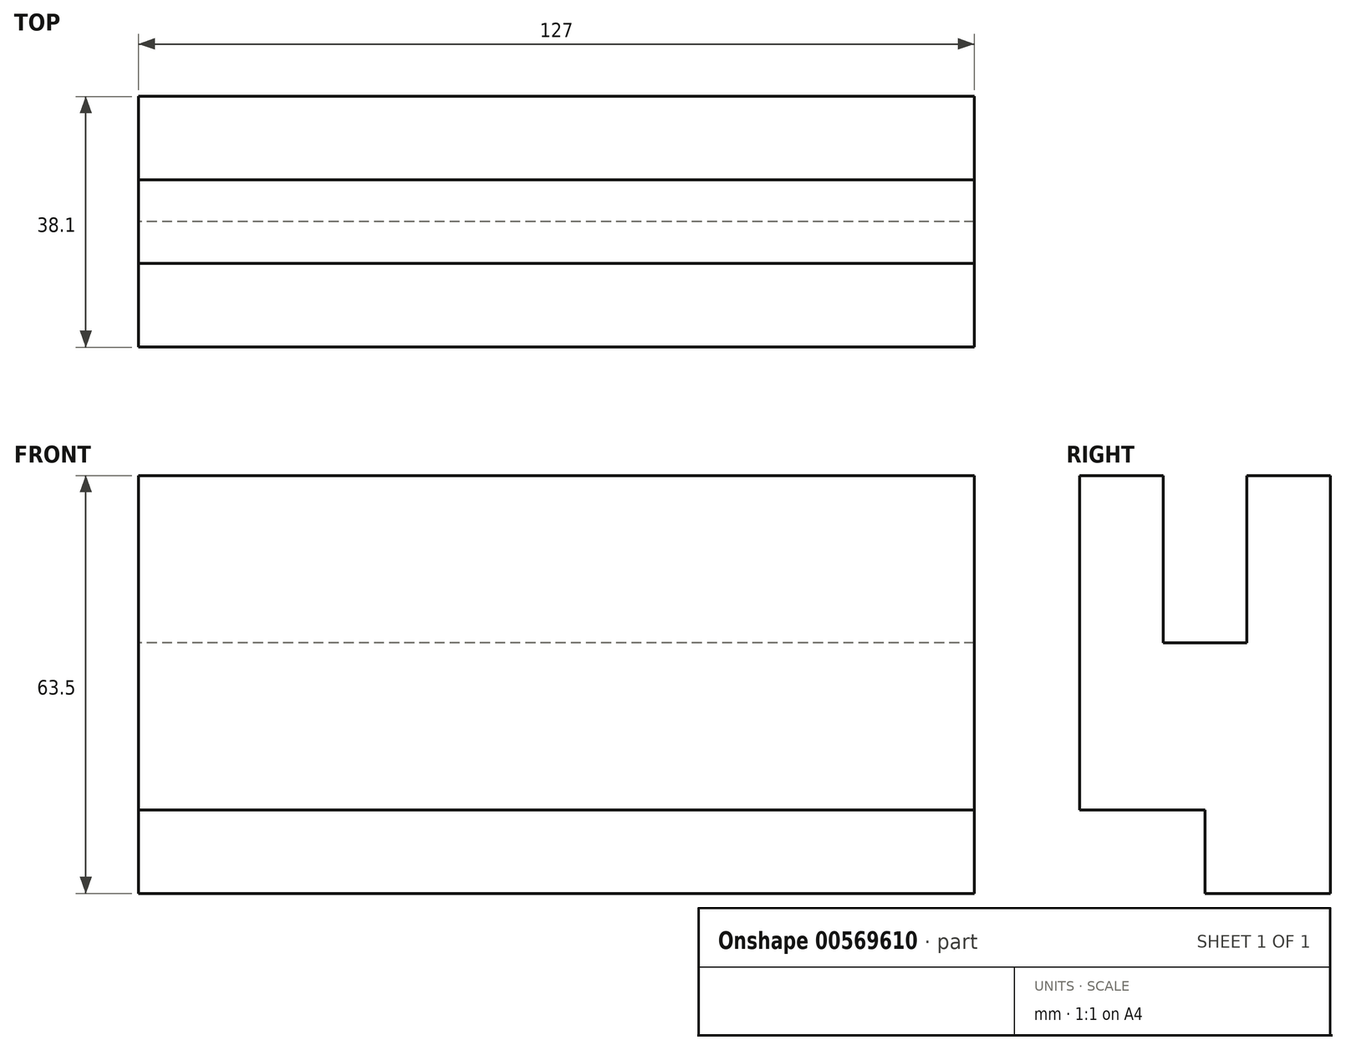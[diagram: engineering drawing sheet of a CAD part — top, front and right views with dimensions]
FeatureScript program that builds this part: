
annotation { "Feature Type Name" : "Feature", "Feature Type Description" : "" }
export const myFeature = defineFeature(function(context is Context, id is Id, definition is map)
    precondition{}
    {
        {
            var Q0;
            Q0=qCreatedBy(makeId("Right.planeOp"),FACE);
            var sketch = newSketch(context, id + "F0", { "sketchPlane" : qUnion([Q0])});
            skLineSegment(sketch, "E0", {"start": v(-39.45, 50.8) * mm, "end": v(-26.75, 50.8) * mm});
            skLineSegment(sketch, "E1", {"start": v(-26.75, 50.8) * mm, "end": v(-26.75, 25.4) * mm});
            skLineSegment(sketch, "E2", {"start": v(-14.05, 25.4) * mm, "end": v(-14.05, 50.8) * mm});
            skLineSegment(sketch, "E3", {"start": v(-14.05, 50.8) * mm, "end": v(-14.05, 25.4) * mm});
            skLineSegment(sketch, "E4", {"start": v(-26.75, 25.4) * mm, "end": v(-14.05, 25.4) * mm});
            skLineSegment(sketch, "E5", {"start": v(-14.05, 50.8) * mm, "end": v(-1.35, 50.8) * mm});
            skLineSegment(sketch, "E6", {"start": v(-1.35, 50.8) * mm, "end": v(-1.35, -12.7) * mm});
            skLineSegment(sketch, "E7", {"start": v(-1.35, -12.7) * mm, "end": v(-20.4, -12.7) * mm});
            skLineSegment(sketch, "E8", {"start": v(-20.4, -12.7) * mm, "end": v(-20.4, 0) * mm});
            skLineSegment(sketch, "E9", {"start": v(-20.4, 0) * mm, "end": v(-39.45, 0) * mm});
            skLineSegment(sketch, "E10", {"start": v(-39.45, 50.8) * mm, "end": v(-39.45, 0) * mm});
            skSolve(sketch);
        }
        {
            var Q0;
            Q0 = qSketchRegion(id + "F0", true);
            extrude(context, id + "F1", {"entities" : qUnion([Q0]), "depth" : 127 * mm, "offsetDistance" : 25.4 * mm});
        }
    });
